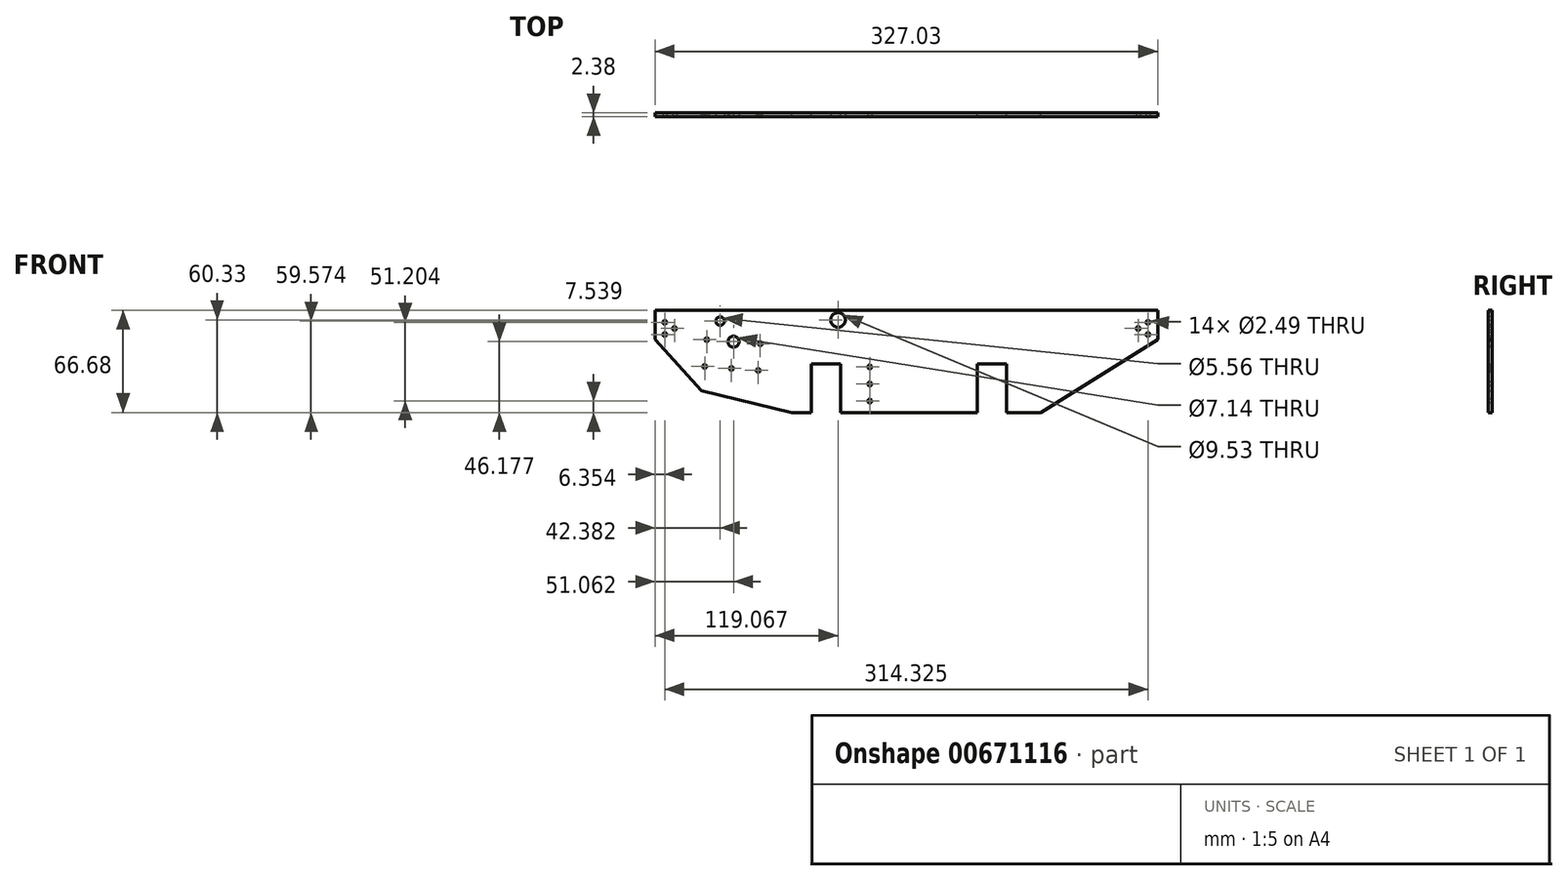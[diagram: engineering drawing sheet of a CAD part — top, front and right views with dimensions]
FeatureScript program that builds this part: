
annotation { "Feature Type Name" : "Feature", "Feature Type Description" : "" }
export const myFeature = defineFeature(function(context is Context, id is Id, definition is map)
    precondition{}
    {
        {
            var Q0;
            Q0=qCreatedBy(makeId("Front.planeOp"),FACE);
            var sketch = newSketch(context, id + "F0", { "sketchPlane" : qUnion([Q0])});
            skLineSegment(sketch, "E0", {"start": v(-44.67, 19.05) * mm, "end": v(282.36, 19.05) * mm});
            skLineSegment(sketch, "E1", {"start": v(282.36, 19.05) * mm, "end": v(282.36, 0) * mm});
            skLineSegment(sketch, "E2", {"start": v(282.36, 0) * mm, "end": v(206.16, -47.63) * mm});
            skLineSegment(sketch, "E3", {"start": v(206.16, -47.63) * mm, "end": v(183.93, -47.63) * mm});
            skLineSegment(sketch, "E4", {"start": v(183.93, -47.63) * mm, "end": v(183.93, -15.88) * mm});
            skLineSegment(sketch, "E5", {"start": v(183.93, -15.88) * mm, "end": v(164.88, -15.88) * mm});
            skLineSegment(sketch, "E6", {"start": v(164.88, -15.88) * mm, "end": v(164.88, -47.63) * mm});
            skLineSegment(sketch, "E7", {"start": v(164.88, -47.63) * mm, "end": v(75.98, -47.63) * mm});
            skLineSegment(sketch, "E8", {"start": v(75.98, -47.63) * mm, "end": v(75.98, -15.88) * mm});
            skLineSegment(sketch, "E9", {"start": v(75.98, -15.88) * mm, "end": v(56.93, -15.88) * mm});
            skLineSegment(sketch, "E10", {"start": v(56.93, -15.88) * mm, "end": v(56.93, -47.63) * mm});
            skLineSegment(sketch, "E11", {"start": v(56.93, -47.63) * mm, "end": v(44.23, -47.63) * mm});
            skLineSegment(sketch, "E12", {"start": v(44.23, -47.63) * mm, "end": v(-14.5, -33.4) * mm});
            skLineSegment(sketch, "E13", {"start": v(-14.5, -33.4) * mm, "end": v(-44.67, 0) * mm});
            skLineSegment(sketch, "E14", {"start": v(-44.67, 0) * mm, "end": v(-44.67, 19.05) * mm});
            skSolve(sketch);
        }
        {
            var Q0;
            Q0=qSketchRegion(id+"F0",true);
            extrude(context, id + "F1", {"entities" : qUnion([Q0]), "depth" : 2.38 * mm});
        }
        {
            var Q0;
            Q0=makeQuery(id+"F1.opExtrude","CAP_FACE",FACE,{"disambiguationData":[OSD([sQuery(id+"F0.wireOp",EDGE,"E0"),sQuery(id+"F0.wireOp",EDGE,"E1"),sQuery(id+"F0.wireOp",EDGE,"E2"),sQuery(id+"F0.wireOp",EDGE,"E3"),sQuery(id+"F0.wireOp",EDGE,"E4"),sQuery(id+"F0.wireOp",EDGE,"E5"),sQuery(id+"F0.wireOp",EDGE,"E6"),sQuery(id+"F0.wireOp",EDGE,"E7"),sQuery(id+"F0.wireOp",EDGE,"E8"),sQuery(id+"F0.wireOp",EDGE,"E9"),sQuery(id+"F0.wireOp",EDGE,"E10"),sQuery(id+"F0.wireOp",EDGE,"E11"),sQuery(id+"F0.wireOp",EDGE,"E12"),sQuery(id+"F0.wireOp",EDGE,"E13"),sQuery(id+"F0.wireOp",EDGE,"E14")])],"isStart":false});
            var sketch = newSketch(context, id + "F2", { "sketchPlane" : qUnion([Q0])});
            skCircle(sketch, "E15", {"center": v(276, 11.11) * mm, "radius": 1.24 * mm});
            skCircle(sketch, "E16", {"center": v(276, 3.17) * mm, "radius": 1.24 * mm});
            skCircle(sketch, "E17", {"center": v(269.66, 7.14) * mm, "radius": 1.24 * mm});
            skCircle(sketch, "E18", {"center": v(74.4, 12.7) * mm, "radius": 4.76 * mm});
            skCircle(sketch, "E19", {"center": v(95.03, -17.87) * mm, "radius": 1.24 * mm});
            skCircle(sketch, "E20", {"center": v(95.03, -28.98) * mm, "radius": 1.24 * mm});
            skCircle(sketch, "E21", {"center": v(95.03, -40.1) * mm, "radius": 1.24 * mm});
            skCircle(sketch, "E22", {"center": v(-38.32, 11.11) * mm, "radius": 1.24 * mm});
            skCircle(sketch, "E23", {"center": v(-38.32, 3.17) * mm, "radius": 1.24 * mm});
            skCircle(sketch, "E24", {"center": v(-31.97, 7.14) * mm, "radius": 1.24 * mm});
            skPoint(sketch, "E25", {"position": v(174.4, -31.75) * mm});
            skLineSegment(sketch, "E26", {"start": v(174.4, -31.75) * mm, "end": v(-44.67, -15.08) * mm});
            skCircle(sketch, "E27", {"center": v(-12.34, -17.54) * mm, "radius": 1.24 * mm});
            skCircle(sketch, "E28", {"center": v(5.07, -18.87) * mm, "radius": 1.24 * mm});
            skCircle(sketch, "E29", {"center": v(22.48, -20.2) * mm, "radius": 1.24 * mm});
            skCircle(sketch, "E30", {"center": v(-11.02, -0.13) * mm, "radius": 1.24 * mm});
            skCircle(sketch, "E31", {"center": v(23.8, -2.78) * mm, "radius": 1.24 * mm});
            skCircle(sketch, "E32", {"center": v(6.4, -1.45) * mm, "radius": 3.57 * mm});
            skCircle(sketch, "E33", {"center": v(-2.29, 11.94) * mm, "radius": 2.78 * mm});
            skLineSegment(sketch, "E34", {"start": v(-44.67, -15.08) * mm, "end": v(-42.74, 10.26) * mm});
            skLineSegment(sketch, "E35", {"start": v(-12.34, -17.54) * mm, "end": v(-10.66, 4.63) * mm});
            skSolve(sketch);
        }
        {
            var Q0;
            Q0=qSketchRegion(id+"F2",true);
            extrude(context, id + "F3", {"entities" : qUnion([Q0]), "operationType" : NewBodyOperationType.REMOVE, "oppositeDirection" : true, "depth" : 2.38 * mm});
        }
    });
